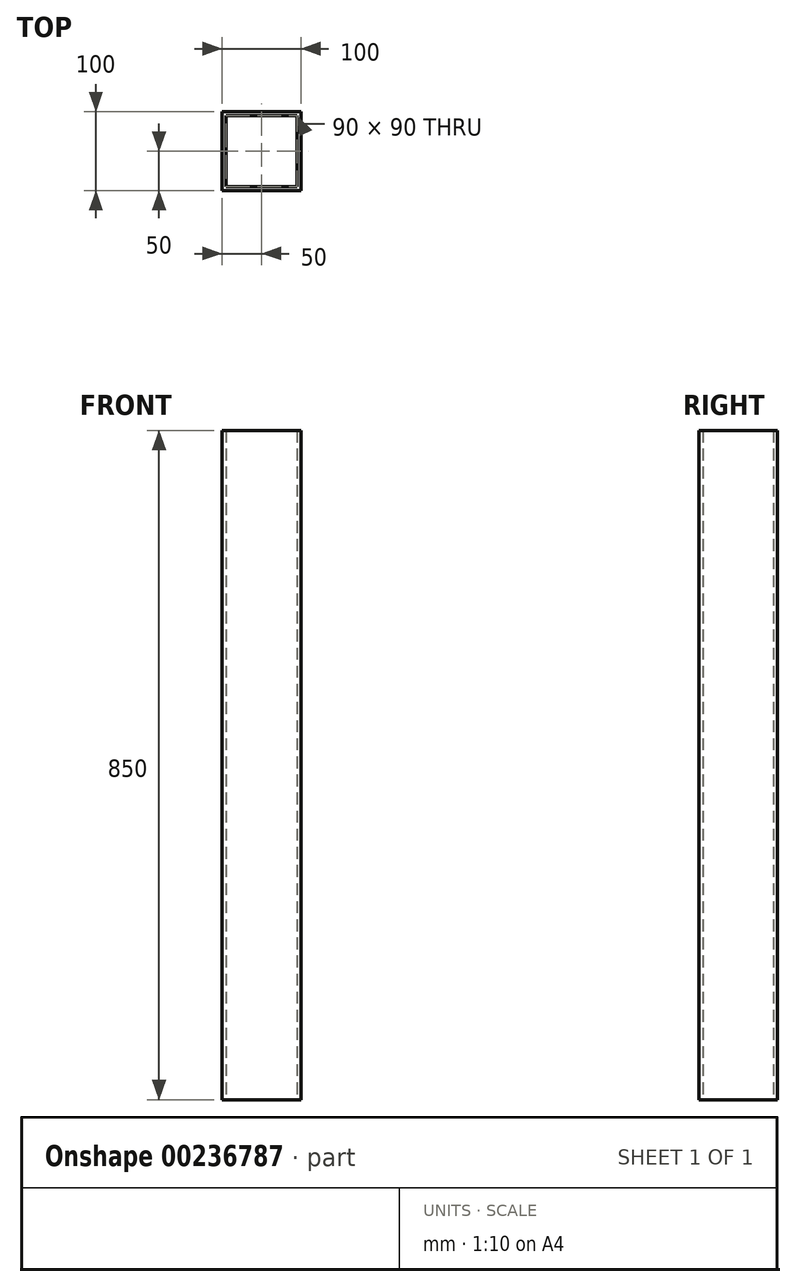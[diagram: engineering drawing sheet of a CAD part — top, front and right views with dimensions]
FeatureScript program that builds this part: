
annotation { "Feature Type Name" : "Feature", "Feature Type Description" : "" }
export const myFeature = defineFeature(function(context is Context, id is Id, definition is map)
    precondition{}
    {
        {
            var Q0;
            Q0=qCreatedBy(makeId("Top.planeOp"),FACE);
            var sketch = newSketch(context, id + "F0", { "sketchPlane" : qUnion([Q0])});
            skLineSegment(sketch, "E0.bottom", {"start": v(0, 0) * mm, "end": v(100, 0) * mm});
            skLineSegment(sketch, "E0.top", {"start": v(0, 100) * mm, "end": v(100, 100) * mm});
            skLineSegment(sketch, "E0.left", {"start": v(0, 0) * mm, "end": v(0, 100) * mm});
            skLineSegment(sketch, "E0.right", {"start": v(100, 0) * mm, "end": v(100, 100) * mm});
            skLineSegment(sketch, "E1.bottom", {"start": v(5, 95) * mm, "end": v(95, 95) * mm});
            skLineSegment(sketch, "E1.top", {"start": v(5, 5) * mm, "end": v(95, 5) * mm});
            skLineSegment(sketch, "E1.left", {"start": v(5, 95) * mm, "end": v(5, 5) * mm});
            skLineSegment(sketch, "E1.right", {"start": v(95, 95) * mm, "end": v(95, 5) * mm});
            skSolve(sketch);
        }
        {
            var Q0;
            Q0 = qSketchRegion(id + "F0", true);
            extrude(context, id + "F1", {"entities" : qUnion([Q0]), "depth" : 850 * mm, "offsetDistance" : 25 * mm});
        }
    });
